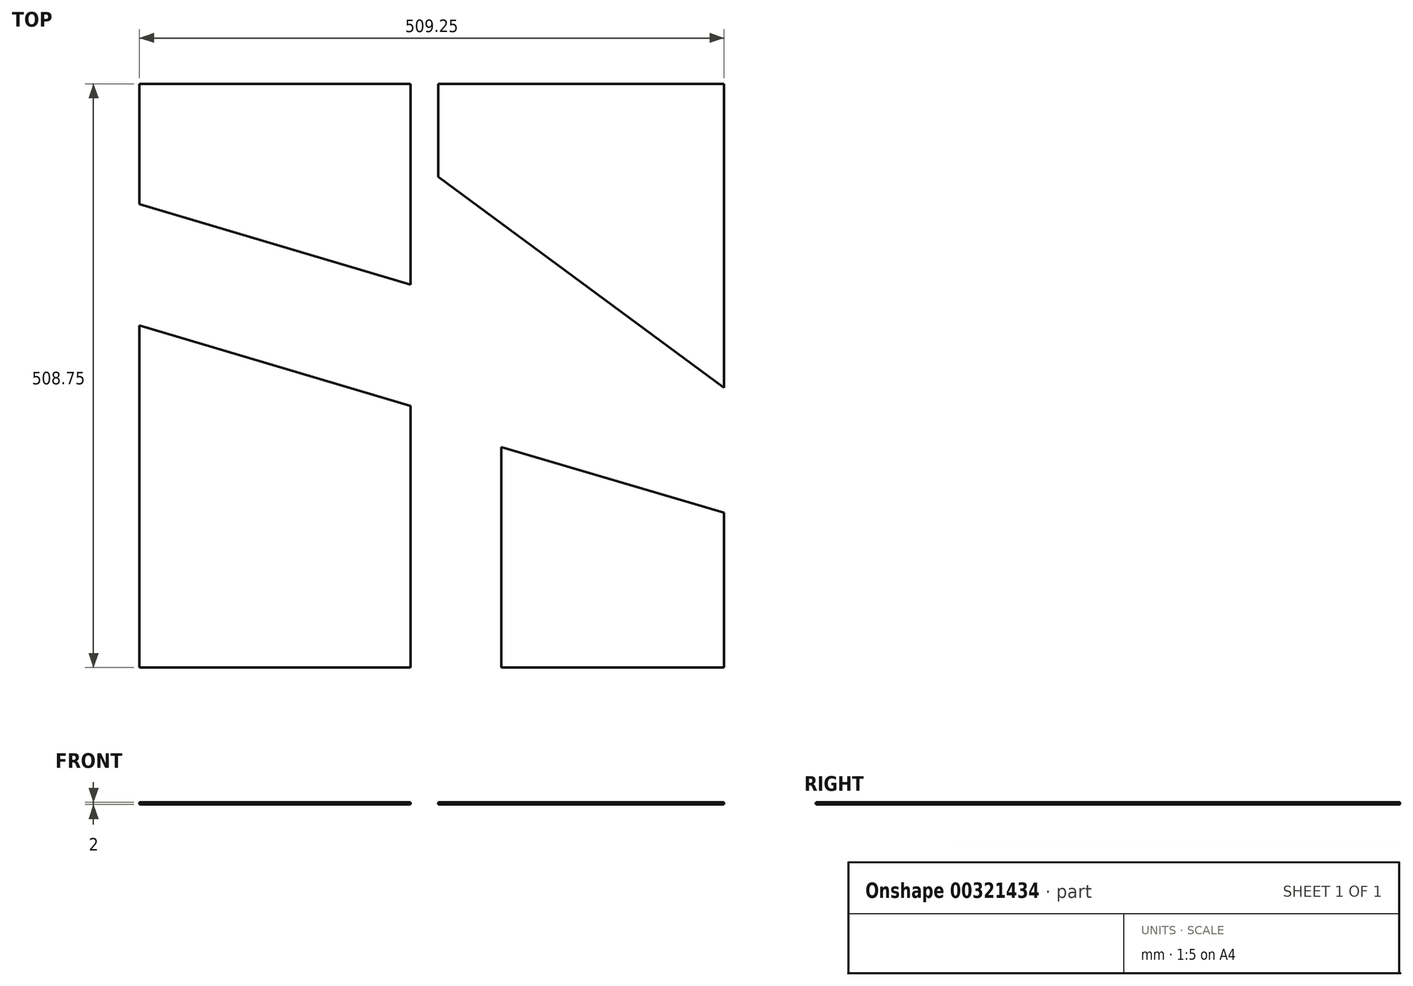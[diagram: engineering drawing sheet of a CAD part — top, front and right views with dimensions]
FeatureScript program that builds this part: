
annotation { "Feature Type Name" : "Feature", "Feature Type Description" : "" }
export const myFeature = defineFeature(function(context is Context, id is Id, definition is map)
    precondition{}
    {
        {
            var Q0;
            Q0=qCreatedBy(makeId("Top.planeOp"),FACE);
            var sketch = newSketch(context, id + "F0", { "sketchPlane" : qUnion([Q0])});
            skLineSegment(sketch, "E0", {"start": v(-262.9, 95.96) * mm, "end": v(-262.9, -202.04) * mm});
            skLineSegment(sketch, "E1", {"start": v(-262.9, -202.04) * mm, "end": v(-26.9, -202.04) * mm});
            skLineSegment(sketch, "E2", {"start": v(-26.9, -202.04) * mm, "end": v(-26.9, 25.96) * mm});
            skLineSegment(sketch, "E3", {"start": v(-26.9, 25.96) * mm, "end": v(-262.9, 95.96) * mm});
            skLineSegment(sketch, "E4", {"start": v(52.34, -202.04) * mm, "end": v(52.34, -10.04) * mm});
            skLineSegment(sketch, "E5", {"start": v(52.34, -10.04) * mm, "end": v(246.34, -67.04) * mm});
            skLineSegment(sketch, "E6", {"start": v(246.34, -67.04) * mm, "end": v(246.34, -202.04) * mm});
            skLineSegment(sketch, "E7", {"start": v(246.34, -202.04) * mm, "end": v(52.34, -202.04) * mm});
            skLineSegment(sketch, "E8", {"start": v(246.34, 41.71) * mm, "end": v(246.34, 306.71) * mm});
            skLineSegment(sketch, "E9", {"start": v(246.34, 306.71) * mm, "end": v(-2.66, 306.71) * mm});
            skLineSegment(sketch, "E10", {"start": v(-2.66, 306.71) * mm, "end": v(-2.66, 225.71) * mm});
            skLineSegment(sketch, "E11", {"start": v(-2.66, 225.71) * mm, "end": v(246.34, 41.71) * mm});
            skLineSegment(sketch, "E12", {"start": v(-262.9, 306.71) * mm, "end": v(-26.9, 306.71) * mm});
            skLineSegment(sketch, "E13", {"start": v(-26.9, 306.71) * mm, "end": v(-26.9, 131.71) * mm});
            skLineSegment(sketch, "E14", {"start": v(-26.9, 131.71) * mm, "end": v(-262.9, 201.71) * mm});
            skLineSegment(sketch, "E15", {"start": v(-262.9, 201.71) * mm, "end": v(-262.9, 306.71) * mm});
            skSolve(sketch);
        }
        {
            var Q0;
            Q0 = qSketchRegion(id + "F0", true);
            extrude(context, id + "F1", {"entities" : qUnion([Q0]), "depth" : 2 * mm});
        }
    });
